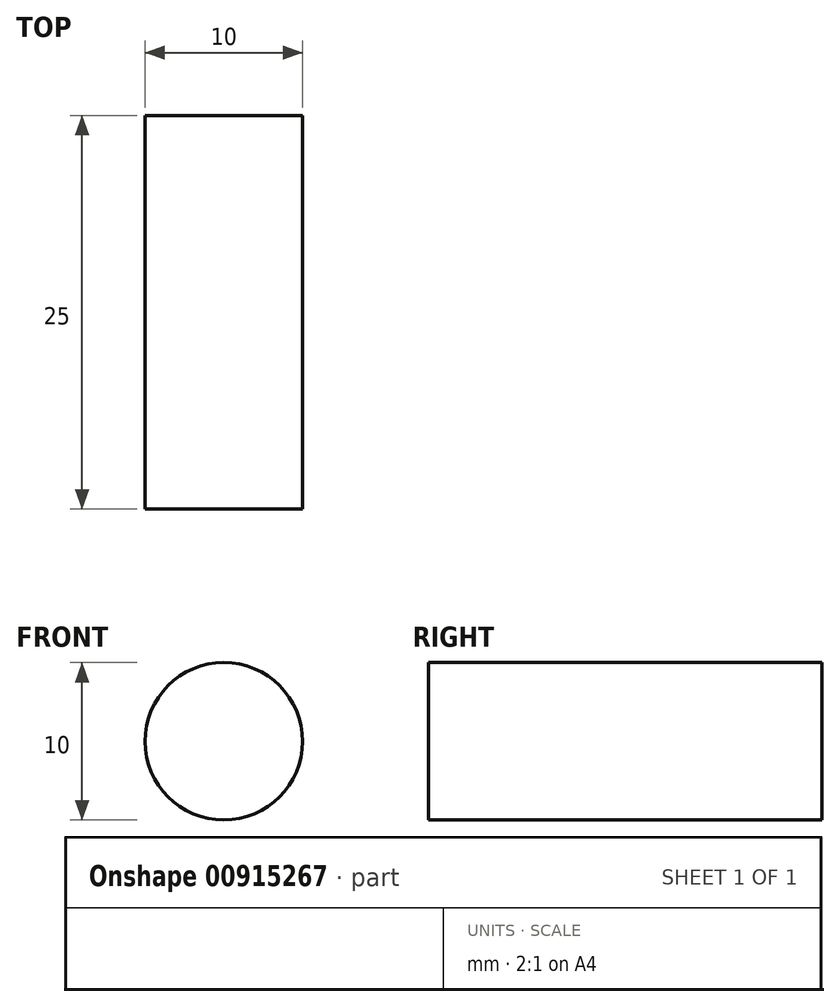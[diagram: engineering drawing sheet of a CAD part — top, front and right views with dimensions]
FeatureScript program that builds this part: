
annotation { "Feature Type Name" : "Feature", "Feature Type Description" : "" }
export const myFeature = defineFeature(function(context is Context, id is Id, definition is map)
    precondition{}
    {
        {
            var Q0;
            Q0=qCreatedBy(makeId("Front.planeOp"),FACE);
            var sketch = newSketch(context, id + "F0", { "sketchPlane" : qUnion([Q0])});
            skCircle(sketch, "E0", {"center": v(0, 0) * mm, "radius": 5 * mm});
            skSolve(sketch);
        }
        {
            var Q0;
            Q0=makeQuery(id+"F0.imprint","IMPRINT",FACE,{"disambiguationData":[TD([[makeQuery(id+"F0.imprint","IMPRINT",EDGE,{"derivedFrom":sQuery(id+"F0.wireOp",EDGE,"E0")}),1.0]])]});
            extrude(context, id + "F1", {"entities" : qUnion([Q0]), "depth" : 25 * mm, "offsetDistance" : 25 * mm});
        }
    });
